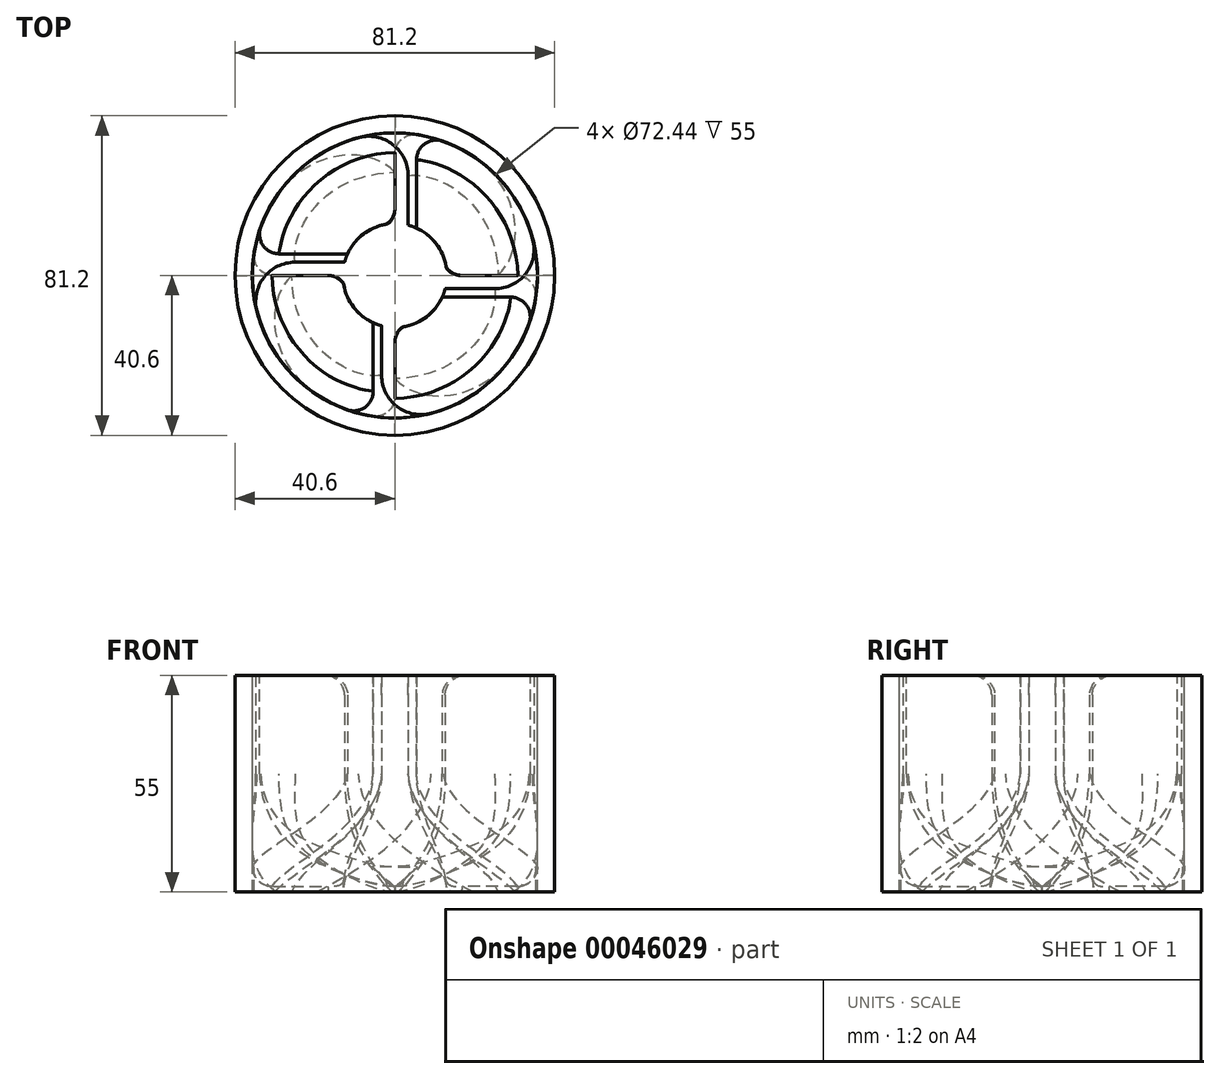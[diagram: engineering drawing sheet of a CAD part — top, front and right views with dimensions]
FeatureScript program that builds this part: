
annotation { "Feature Type Name" : "Feature", "Feature Type Description" : "" }
export const myFeature = defineFeature(function(context is Context, id is Id, definition is map)
    precondition{}
    {
        {
            var Q0;
            Q0=qCreatedBy(makeId("Top.planeOp"),FACE);
            var sketch = newSketch(context, id + "F0", { "sketchPlane" : qUnion([Q0])});
            skLineSegment(sketch, "E0.bottom", {"start": v(-67.42, 5.5) * mm, "end": v(-10.76, 5.5) * mm});
            skLineSegment(sketch, "E0.top", {"start": v(-67.42, 3.36) * mm, "end": v(-10.76, 3.36) * mm});
            skLineSegment(sketch, "E0.left", {"start": v(-67.42, 5.5) * mm, "end": v(-67.42, 3.36) * mm});
            skLineSegment(sketch, "E0.right", {"start": v(-10.76, 5.5) * mm, "end": v(-10.76, 3.36) * mm});
            skSolve(sketch);
        }
        {
            var Q0;
            Q0=qCreatedBy(makeId("Right.planeOp"),FACE);
            cPlane(context, id + "F1", {"entities" : qUnion([Q0]), "cplaneType" : CPlaneType.OFFSET, "offset" : 0 * mm, "width" : 150 * mm, "height" : 150 * mm});
        }
        {
            var Q0;
            Q0=qCreatedBy(id+"F1.planeOp",FACE);
            var sketch = newSketch(context, id + "F2", { "sketchPlane" : qUnion([Q0])});
            skLineSegment(sketch, "E1.bottom", {"start": v(49.68, -28.62) * mm, "end": v(13.6, -28.62) * mm});
            skLineSegment(sketch, "E1.top", {"start": v(49.68, -30) * mm, "end": v(13.6, -30) * mm});
            skLineSegment(sketch, "E1.left", {"start": v(49.68, -28.62) * mm, "end": v(49.68, -30) * mm});
            skLineSegment(sketch, "E1.right", {"start": v(13.6, -28.62) * mm, "end": v(13.6, -30) * mm});
            skSolve(sketch);
        }
        {
            var Q0;
            Q0=makeQuery(id+"F0.imprint","IMPRINT",FACE,{"disambiguationData":[TD([[makeQuery(id+"F0.imprint","IMPRINT",EDGE,{"derivedFrom":sQuery(id+"F0.wireOp",EDGE,"E0.bottom")}),-1.0]])]});
            var Q1;
            Q1=makeQuery(id+"F2.imprint","IMPRINT",FACE,{"disambiguationData":[TD([[makeQuery(id+"F2.imprint","IMPRINT",EDGE,{"derivedFrom":sQuery(id+"F2.wireOp",EDGE,"E1.bottom")}),1.0]])]});
            loft(context, id + "F3", {"startCondition" : LoftEndDerivativeType.NORMAL_TO_PROFILE, "startMagnitude" : 1, "endCondition" : LoftEndDerivativeType.NORMAL_TO_PROFILE, "endMagnitude" : 1, "sheetProfilesArray" : [{ "sheetProfileEntities" : qUnion([Q0]) }, { "sheetProfileEntities" : qUnion([Q1]) }]});
        }
        {
            var Q0;
            Q0=makeQuery(id+"F3.opLoft","CAP_FACE",FACE,{"disambiguationData":[OSD([makeQuery(id+"F0.imprint","IMPRINT",FACE,{"disambiguationData":[TD([[makeQuery(id+"F0.imprint","IMPRINT",EDGE,{"derivedFrom":sQuery(id+"F0.wireOp",EDGE,"E0.bottom")}),-1.0]])]})])],"isStart":true});
            cPlane(context, id + "F4", {"entities" : qUnion([Q0]), "cplaneType" : CPlaneType.OFFSET, "offset" : 0 * mm, "width" : 150 * mm, "height" : 150 * mm});
        }
        {
            var Q0;
            Q0=qCreatedBy(id+"F4.planeOp",FACE);
            var sketch = newSketch(context, id + "F5", { "sketchPlane" : qUnion([Q0])});
            skCircle(sketch, "E2", {"center": v(0, 0) * mm, "radius": 36.22 * mm});
            skCircle(sketch, "E3", {"center": v(0, 0) * mm, "radius": 40.6 * mm});
            skCircle(sketch, "E4", {"center": v(0, 0) * mm, "radius": 74.83 * mm});
            skCircle(sketch, "E5", {"center": v(0, 0) * mm, "radius": 13.22 * mm});
            skSolve(sketch);
        }
        {
            var Q0;
            Q0=makeQuery(id+"F5.imprint","IMPRINT",FACE,{"disambiguationData":[TD([[makeQuery(id+"F5.imprint","IMPRINT",EDGE,{"derivedFrom":sQuery(id+"F5.wireOp",EDGE,"E3")}),-1.0]])]});
            var Q1;
            Q1=makeQuery(id+"F3.opLoft","SWEPT_BODY",BODY,{"disambiguationData":[OSD([makeQuery(id+"F0.imprint","IMPRINT",FACE,{"disambiguationData":[TD([[makeQuery(id+"F0.imprint","IMPRINT",EDGE,{"derivedFrom":sQuery(id+"F0.wireOp",EDGE,"E0.bottom")}),-1.0]])]}),makeQuery(id+"F2.imprint","IMPRINT",FACE,{"disambiguationData":[TD([[makeQuery(id+"F2.imprint","IMPRINT",EDGE,{"derivedFrom":sQuery(id+"F2.wireOp",EDGE,"E1.bottom")}),1.0]])]})])]});
            extrude(context, id + "F6", {"entities" : qUnion([Q0]), "operationType" : NewBodyOperationType.REMOVE, "oppositeDirection" : true, "endBoundEntityBody" : qUnion([Q1]), "depth" : 49 * mm});
        }
        {
            var Q0;
            Q0=makeQuery(id+"F5.imprint","IMPRINT",FACE,{"disambiguationData":[TD([[makeQuery(id+"F5.imprint","IMPRINT",EDGE,{"derivedFrom":sQuery(id+"F5.wireOp",EDGE,"E2")}),-1.0]])]});
            extrude(context, id + "F7", {"entities" : qUnion([Q0]), "operationType" : NewBodyOperationType.ADD, "oppositeDirection" : true, "depth" : 30 * mm});
        }
        {
            var Q0;
            Q0=makeQuery(id+"F3.opLoft","MID_CAP_EDGE",EDGE,{"disambiguationData":[OSD([sQuery(id+"F2.wireOp",EDGE,"E1.bottom"),sQuery(id+"F2.wireOp",EDGE,"E1.top"),sQuery(id+"F2.wireOp",EDGE,"E1.right")])],"capPos":1.0});
            fillet(context, id + "F8", {"entities" : qUnion([Q0]), "radius" : 5 * mm, "allowEdgeOverflow" : false});
        }
        {
            var Q0;
            Q0=makeQuery(id+"F7.boolean.opBoolean","INTERSECT",EDGE,{"derivedFrom":[makeQuery(id+"F3.opLoft","SWEPT_FACE",FACE,{"disambiguationData":[OSD([sQuery(id+"F0.wireOp",EDGE,"E0.top"),sQuery(id+"F0.wireOp",EDGE,"E0.left"),sQuery(id+"F0.wireOp",EDGE,"E0.right"),sQuery(id+"F2.wireOp",EDGE,"E1.top"),sQuery(id+"F2.wireOp",EDGE,"E1.left"),sQuery(id+"F2.wireOp",EDGE,"E1.right")])]}),makeQuery(id+"F7.opExtrude","SWEPT_FACE",FACE,{"disambiguationData":[OSD([sQuery(id+"F5.wireOp",EDGE,"E2")])]})]});
            fillet(context, id + "F9", {"entities" : qUnion([Q0]), "radius" : 10 * mm, "tangentPropagation" : true, "allowEdgeOverflow" : false});
        }
        {
            var Q0;
            Q0=makeQuery(id+"F5.imprint","IMPRINT",FACE,{"disambiguationData":[TD([[makeQuery(id+"F5.imprint","IMPRINT",EDGE,{"derivedFrom":sQuery(id+"F5.wireOp",EDGE,"E5")}),1.0]])]});
            extrude(context, id + "F10", {"entities" : qUnion([Q0]), "operationType" : NewBodyOperationType.REMOVE, "oppositeDirection" : true, "depth" : 40 * mm});
        }
        {
            var Q0;
            Q0=makeQuery(id+"F7.boolean.opBoolean","MERGE",FACE,{"derivedFrom":[makeQuery(id+"F3.opLoft","CAP_FACE",FACE,{"disambiguationData":[OSD([makeQuery(id+"F0.imprint","IMPRINT",FACE,{"disambiguationData":[TD([[makeQuery(id+"F0.imprint","IMPRINT",EDGE,{"derivedFrom":sQuery(id+"F0.wireOp",EDGE,"E0.bottom")}),-1.0]])]})])],"isStart":true}),makeQuery(id+"F7.opExtrude","CAP_FACE",FACE,{"disambiguationData":[OSD([sQuery(id+"F5.wireOp",EDGE,"E2"),sQuery(id+"F5.wireOp",EDGE,"E3")])],"isStart":true})]});
            extrude(context, id + "F11", {"entities" : qUnion([Q0]), "operationType" : NewBodyOperationType.ADD, "depth" : 25 * mm});
        }
        {
            var Q0;
            Q0=qCreatedBy(makeId("Right.planeOp"),FACE);
            var sketch = newSketch(context, id + "F12", { "sketchPlane" : qUnion([Q0])});
            skLineSegment(sketch, "E6", {"start": v(0, 0) * mm, "end": v(0, -66.51) * mm, "construction": true});
            skSolve(sketch);
        }
        {
            var Q0;
            Q0=makeQuery(id+"F7.boolean.opBoolean","INTERSECT",EDGE,{"derivedFrom":[makeQuery(id+"F3.opLoft","SWEPT_FACE",FACE,{"disambiguationData":[OSD([sQuery(id+"F0.wireOp",EDGE,"E0.bottom"),sQuery(id+"F0.wireOp",EDGE,"E0.left"),sQuery(id+"F0.wireOp",EDGE,"E0.right"),sQuery(id+"F2.wireOp",EDGE,"E1.bottom"),sQuery(id+"F2.wireOp",EDGE,"E1.left"),sQuery(id+"F2.wireOp",EDGE,"E1.right")])]}),makeQuery(id+"F7.opExtrude","SWEPT_FACE",FACE,{"disambiguationData":[OSD([sQuery(id+"F5.wireOp",EDGE,"E2")])]})]});
            var Q1;
            Q1=makeQuery(id+"F11.opExtrude","SWEPT_EDGE",EDGE,{"disambiguationData":[OSD([sQuery(id+"F0.wireOp",EDGE,"E0.bottom"),sQuery(id+"F0.wireOp",EDGE,"E0.left"),sQuery(id+"F0.wireOp",EDGE,"E0.right"),sQuery(id+"F2.wireOp",EDGE,"E1.bottom"),sQuery(id+"F2.wireOp",EDGE,"E1.left"),sQuery(id+"F2.wireOp",EDGE,"E1.right"),sQuery(id+"F5.wireOp",EDGE,"E2")])]});
            var Q2;
            Q2=makeQuery(id+"F7.boolean.opBoolean","INTERSECT",EDGE,{"derivedFrom":[makeQuery(id+"F3.opLoft","CAP_FACE",FACE,{"disambiguationData":[OSD([makeQuery(id+"F2.imprint","IMPRINT",FACE,{"disambiguationData":[TD([[makeQuery(id+"F2.imprint","IMPRINT",EDGE,{"derivedFrom":sQuery(id+"F2.wireOp",EDGE,"E1.bottom")}),1.0]])]})])],"isStart":true}),makeQuery(id+"F7.opExtrude","SWEPT_FACE",FACE,{"disambiguationData":[OSD([sQuery(id+"F5.wireOp",EDGE,"E2")])]})]});
            fillet(context, id + "F13", {"entities" : qUnion([Q0, Q1, Q2]), "radius" : 5 * mm, "tangentPropagation" : true, "allowEdgeOverflow" : false});
        }
        {
            var Q0;
            Q0=makeQuery(id+"F11.opExtrude","CAP_EDGE",EDGE,{"disambiguationData":[OSD([sQuery(id+"F5.wireOp",EDGE,"E5")])],"isStart":false});
            fillet(context, id + "F14", {"entities" : qUnion([Q0]), "radius" : 5 * mm, "tangentPropagation" : true, "allowEdgeOverflow" : false});
        }
        {
            var Q0;
            Q0=makeQuery(id+"F3.opLoft","SWEPT_BODY",BODY,{"disambiguationData":[OSD([makeQuery(id+"F0.imprint","IMPRINT",FACE,{"disambiguationData":[TD([[makeQuery(id+"F0.imprint","IMPRINT",EDGE,{"derivedFrom":sQuery(id+"F0.wireOp",EDGE,"E0.bottom")}),-1.0]])]}),makeQuery(id+"F2.imprint","IMPRINT",FACE,{"disambiguationData":[TD([[makeQuery(id+"F2.imprint","IMPRINT",EDGE,{"derivedFrom":sQuery(id+"F2.wireOp",EDGE,"E1.bottom")}),1.0]])]})])]});
            var Q1;
            Q1=sQuery(id+"F12.wireOp",EDGE,"E6");
            circularPattern(context, id + "F15", {"entities" : qUnion([Q0]), "axis" : qUnion([Q1]), "angle" : 90 * degree, "instanceCount" : 4});
        }
    });
